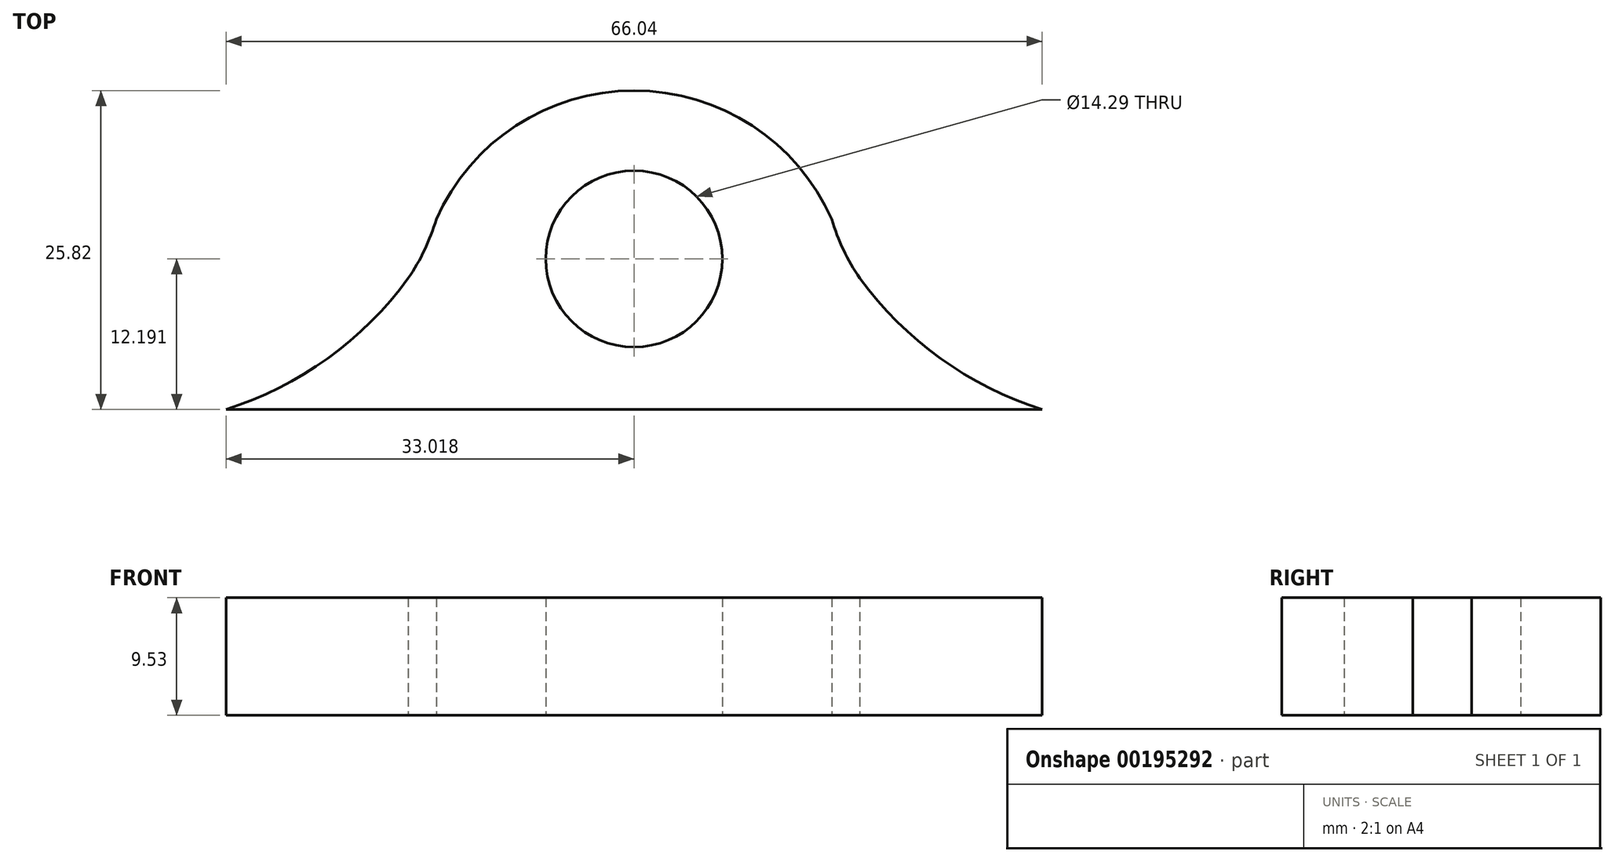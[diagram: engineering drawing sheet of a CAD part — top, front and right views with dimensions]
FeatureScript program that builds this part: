
annotation { "Feature Type Name" : "Feature", "Feature Type Description" : "" }
export const myFeature = defineFeature(function(context is Context, id is Id, definition is map)
    precondition{}
    {
        {
            var Q0;
            Q0=qCreatedBy(makeId("Top.planeOp"),FACE);
            var sketch = newSketch(context, id + "F0", { "sketchPlane" : qUnion([Q0])});
            skLineSegment(sketch, "E0", {"start": v(2.59, -3.42) * mm, "end": v(-38.05, -3.42) * mm});
            skLineSegment(sketch, "E1", {"start": v(-17.73, -3.42) * mm, "end": v(-17.73, 29.4) * mm, "construction": true});
            skCircle(sketch, "E2", {"center": v(-17.73, 8.77) * mm, "radius": 7.14 * mm});
            skCircle(sketch, "E3", {"center": v(-17.73, 8.77) * mm, "radius": 8.9 * mm, "construction": true});
            skLineSegment(sketch, "E4", {"start": v(-43.13, -3.42) * mm, "end": v(-50.75, -3.42) * mm});
            skLineSegment(sketch, "E5", {"start": v(7.67, -3.42) * mm, "end": v(15.29, -3.42) * mm});
            skArc(sketch, "E6", {"start": v(-50.75, -3.42) * mm, "mid": v(-42.53, 0.71) * mm, "end": v(-36, 7.2) * mm});
            skArc(sketch, "E7", {"start": v(0.54, 7.2) * mm, "mid": v(7.07, 0.71) * mm, "end": v(15.29, -3.42) * mm});
            skPoint(sketch, "E8.orphan", {"position": v(-40.45, -3.42) * mm});
            skPoint(sketch, "E9.orphan", {"position": v(4.99, -3.42) * mm});
            skArc(sketch, "E10", {"start": v(-1.73, 11.97) * mm, "mid": v(-17.73, 22.4) * mm, "end": v(-33.74, 11.97) * mm});
            skPoint(sketch, "E11.orphan", {"position": v(-0.84, 9.28) * mm});
            skPoint(sketch, "E12.orphan", {"position": v(-34.62, 9.28) * mm});
            skArc(sketch, "E13", {"start": v(-36, 7.2) * mm, "mid": v(-34.68, 9.5) * mm, "end": v(-33.74, 11.97) * mm});
            skArc(sketch, "E14.MirrorCS", {"start": v(0.54, 7.2) * mm, "mid": v(-0.78, 9.5) * mm, "end": v(-1.73, 11.97) * mm});
            skLineSegment(sketch, "E15", {"start": v(7.67, -3.42) * mm, "end": v(2.59, -3.42) * mm});
            skLineSegment(sketch, "E16", {"start": v(-38.05, -3.42) * mm, "end": v(-43.13, -3.42) * mm});
            skSolve(sketch);
        }
        {
            var Q0;
            Q0=makeQuery(id+"F0.imprint","IMPRINT",FACE,{"disambiguationData":[TD([[makeQuery(id+"F0.imprint","IMPRINT",EDGE,{"derivedFrom":sQuery(id+"F0.wireOp",EDGE,"E0")}),-1.0]])]});
            extrude(context, id + "F1", {"entities" : qUnion([Q0]), "depth" : 9.52 * mm});
        }
        {
            var Q0;
            Q0=makeQuery(id+"F1.opExtrude","CAP_FACE",FACE,{"disambiguationData":[OSD([sQuery(id+"F0.wireOp",EDGE,"E0"),sQuery(id+"F0.wireOp",EDGE,"E2"),sQuery(id+"F0.wireOp",EDGE,"E4"),sQuery(id+"F0.wireOp",EDGE,"E5"),sQuery(id+"F0.wireOp",EDGE,"E6"),sQuery(id+"F0.wireOp",EDGE,"E7"),sQuery(id+"F0.wireOp",EDGE,"jRT7sIB3-eYmv-982z-dszW-tsilm7izs5Ok.top"),sQuery(id+"F0.wireOp",EDGE,"jRT7sIB3-eYmv-982z-dszW-tsilm7izs5Ok.left"),sQuery(id+"F0.wireOp",EDGE,"jRT7sIB3-eYmv-982z-dszW-tsilm7izs5Ok.right"),sQuery(id+"F0.wireOp",EDGE,"AToDTv4n-V2pk-cibX-iMQt-tPWehI7cu3UN.top"),sQuery(id+"F0.wireOp",EDGE,"AToDTv4n-V2pk-cibX-iMQt-tPWehI7cu3UN.left"),sQuery(id+"F0.wireOp",EDGE,"AToDTv4n-V2pk-cibX-iMQt-tPWehI7cu3UN.right"),sQuery(id+"F0.wireOp",EDGE,"E10"),sQuery(id+"F0.wireOp",EDGE,"E13"),sQuery(id+"F0.wireOp",EDGE,"E14.MirrorCS")])],"isStart":false});
            var sketch = newSketch(context, id + "F2", { "sketchPlane" : qUnion([Q0])});
            skCircle(sketch, "E17", {"center": v(-17.73, 8.77) * mm, "radius": 8.73 * mm});
            skSolve(sketch);
        }
    });
